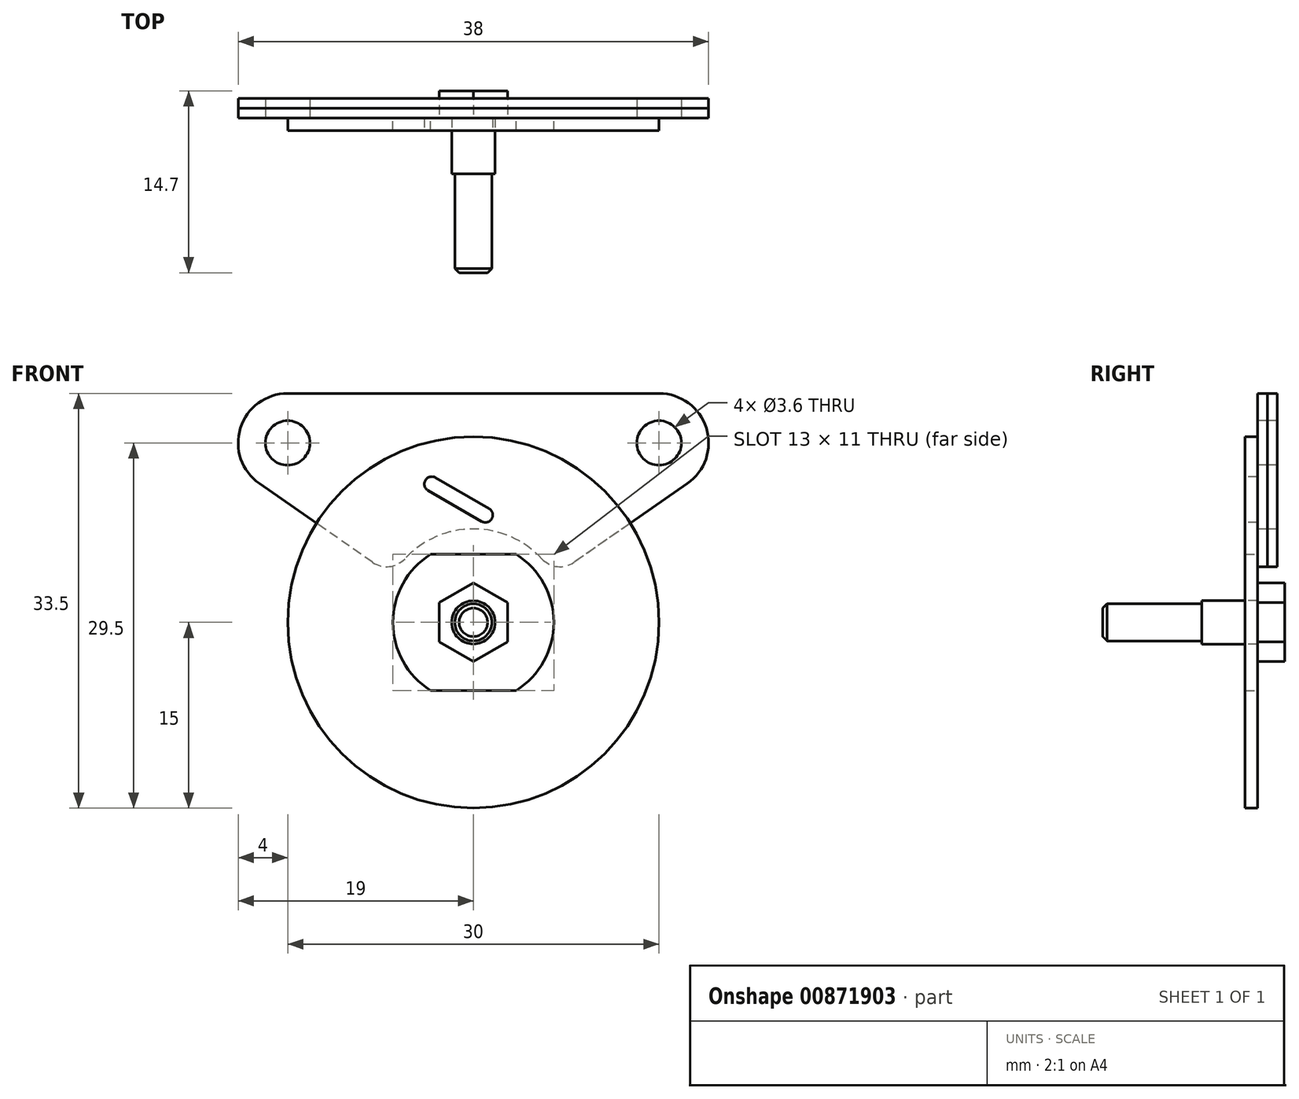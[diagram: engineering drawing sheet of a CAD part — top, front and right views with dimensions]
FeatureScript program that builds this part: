
annotation { "Feature Type Name" : "Feature", "Feature Type Description" : "" }
export const myFeature = defineFeature(function(context is Context, id is Id, definition is map)
    precondition{}
    {
        {
            var Q0;
            Q0=qCreatedBy(makeId("Front.planeOp"),FACE);
            var sketch = newSketch(context, id + "F0", { "sketchPlane" : qUnion([Q0])});
            skCircle(sketch, "E0", {"center": v(0, 0) * mm, "radius": 15 * mm});
            skArc(sketch, "E1", {"start": v(-3.46, 5.5) * mm, "mid": v(-6.5, 0) * mm, "end": v(-3.46, -5.5) * mm});
            skLineSegment(sketch, "E2", {"start": v(0, 0) * mm, "end": v(-24.22, 0) * mm, "construction": true});
            skLineSegment(sketch, "E3", {"start": v(-3.46, 5.5) * mm, "end": v(3.46, 5.5) * mm});
            skLineSegment(sketch, "E4", {"start": v(3.46, -5.5) * mm, "end": v(-3.46, -5.5) * mm});
            skArc(sketch, "E5.trimOffspring", {"start": v(3.46, -5.5) * mm, "mid": v(6.5, 0) * mm, "end": v(3.46, 5.5) * mm});
            skSolve(sketch);
        }
        {
            var Q0;
            Q0=qSketchRegion(id+"F0",true);
            extrude(context, id + "F1", {"entities" : qUnion([Q0]), "depth" : 1 * mm, "offsetDistance" : 25 * mm});
        }
        {
            var Q0;
            Q0=makeQuery(id+"F1.opExtrude","CAP_FACE",FACE,{"disambiguationData":[OSD([sQuery(id+"F0.wireOp",EDGE,"E0"),sQuery(id+"F0.wireOp",EDGE,"E1"),sQuery(id+"F0.wireOp",EDGE,"E3"),sQuery(id+"F0.wireOp",EDGE,"E4"),sQuery(id+"F0.wireOp",EDGE,"E5.trimOffspring")])],"isStart":false});
            var sketch = newSketch(context, id + "F2", { "sketchPlane" : qUnion([Q0])});
            skLineSegment(sketch, "E6", {"start": v(-3.36, 11.18) * mm, "end": v(0.97, 8.68) * mm, "construction": true});
            skArc(sketch, "E7.0.startCap", {"start": v(-3.66, 10.66) * mm, "mid": v(-3.88, 11.48) * mm, "end": v(-3.06, 11.7) * mm});
            skArc(sketch, "E7.0.endCap", {"start": v(1.27, 9.2) * mm, "mid": v(1.49, 8.38) * mm, "end": v(0.67, 8.16) * mm});
            skLineSegment(sketch, "E7.0.left", {"start": v(-3.06, 11.7) * mm, "end": v(1.27, 9.2) * mm});
            skLineSegment(sketch, "E7.0.right", {"start": v(-3.66, 10.66) * mm, "end": v(0.67, 8.16) * mm});
            skLineSegment(sketch, "E8", {"start": v(-1.2, 9.93) * mm, "end": v(-2.05, 8.46) * mm, "construction": true});
            skSolve(sketch);
        }
        {
            var Q0;
            Q0=qSketchRegion(id+"F2",true);
            extrude(context, id + "F3", {"entities" : qUnion([Q0]), "operationType" : NewBodyOperationType.REMOVE, "oppositeDirection" : true, "depth" : 25 * mm, "offsetDistance" : 25 * mm});
        }
        {
            var Q0;
            Q0=qCreatedBy(makeId("Front.planeOp"),FACE);
            var sketch = newSketch(context, id + "F4", { "sketchPlane" : qUnion([Q0])});
            skLineSegment(sketch, "E9", {"start": v(15, 14.5) * mm, "end": v(-15, 14.5) * mm, "construction": true});
            skLineSegment(sketch, "E10", {"start": v(7, 6.5) * mm, "end": v(-7, 6.5) * mm, "construction": true});
            skArc(sketch, "E11", {"start": v(17.28, 11.22) * mm, "mid": v(18.82, 15.7) * mm, "end": v(15, 18.5) * mm});
            skArc(sketch, "E12", {"start": v(-15, 18.5) * mm, "mid": v(-18.82, 15.7) * mm, "end": v(-17.28, 11.22) * mm});
            skArc(sketch, "E13", {"start": v(-8.14, 4.86) * mm, "mid": v(-6.79, 4.51) * mm, "end": v(-5.53, 5.14) * mm});
            skArc(sketch, "E14", {"start": v(5.53, 5.14) * mm, "mid": v(6.79, 4.51) * mm, "end": v(8.14, 4.86) * mm});
            skCircle(sketch, "E15", {"center": v(15, 14.5) * mm, "radius": 1.8 * mm});
            skCircle(sketch, "E16", {"center": v(-15, 14.5) * mm, "radius": 1.8 * mm});
            skLineSegment(sketch, "E17", {"start": v(15, 14.5) * mm, "end": v(15, 18.5) * mm, "construction": true});
            skLineSegment(sketch, "E18", {"start": v(15, 18.5) * mm, "end": v(-15, 18.5) * mm});
            skLineSegment(sketch, "E19", {"start": v(-15, 18.5) * mm, "end": v(-15, 14.5) * mm, "construction": true});
            skArc(sketch, "E20", {"start": v(5.53, 5.14) * mm, "mid": v(0, 7.55) * mm, "end": v(-5.53, 5.14) * mm});
            skLineSegment(sketch, "E21", {"start": v(0, 14.5) * mm, "end": v(0, 6.5) * mm, "construction": true});
            skLineSegment(sketch, "E22", {"start": v(17.28, 11.22) * mm, "end": v(8.14, 4.86) * mm});
            skLineSegment(sketch, "E23", {"start": v(-8.14, 4.86) * mm, "end": v(-17.28, 11.22) * mm});
            skSolve(sketch);
        }
        {
            var Q0;
            Q0=qSketchRegion(id+"F4",true);
            extrude(context, id + "F5", {"entities" : qUnion([Q0]), "oppositeDirection" : true, "depth" : 0.8 * mm, "offsetDistance" : 25 * mm});
        }
        {
            var Q0;
            Q0=makeQuery(id+"F5.opExtrude","SWEPT_BODY",BODY,{"disambiguationData":[OSD([sQuery(id+"F4.wireOp",EDGE,"E11"),sQuery(id+"F4.wireOp",EDGE,"E12"),sQuery(id+"F4.wireOp",EDGE,"E13"),sQuery(id+"F4.wireOp",EDGE,"E14"),sQuery(id+"F4.wireOp",EDGE,"E15"),sQuery(id+"F4.wireOp",EDGE,"E16"),sQuery(id+"F4.wireOp",EDGE,"E18"),sQuery(id+"F4.wireOp",EDGE,"E20"),sQuery(id+"F4.wireOp",EDGE,"E22"),sQuery(id+"F4.wireOp",EDGE,"E23")])]});
            transform(context, id + "F6", {"entities" : qUnion([Q0]), "transformType" : TransformType.TRANSLATION_3D, "dx" : 0 * mm, "dy" : 0.8 * mm, "dz" : 0 * mm, "makeCopy" : true});
        }
        {
            var Q0;
            Q0=qCreatedBy(makeId("Top.planeOp"),FACE);
            var sketch = newSketch(context, id + "F7", { "sketchPlane" : qUnion([Q0])});
            skLineSegment(sketch, "E24", {"start": v(0, 0) * mm, "end": v(0, -12.5) * mm});
            skLineSegment(sketch, "E25", {"start": v(0, -12.5) * mm, "end": v(-1.5, -12.5) * mm});
            skLineSegment(sketch, "E26", {"start": v(-1.5, -12.5) * mm, "end": v(-1.5, -4.5) * mm});
            skLineSegment(sketch, "E27", {"start": v(-1.5, -4.5) * mm, "end": v(-1.75, -4.5) * mm});
            skLineSegment(sketch, "E28", {"start": v(-1.75, -4.5) * mm, "end": v(-1.75, 0) * mm});
            skLineSegment(sketch, "E29", {"start": v(-1.75, 0) * mm, "end": v(0, 0) * mm});
            skLineSegment(sketch, "E30", {"start": v(0, 0) * mm, "end": v(0, 0.89) * mm, "construction": true});
            skSolve(sketch);
        }
        {
            var Q0;
            Q0=qSketchRegion(id+"F7",true);
            var Q1;
            Q1=sQuery(id+"F7.wireOp",EDGE,"E30");
            revolve(context, id + "F8", {"surfaceOperationType" : NewSurfaceOperationType.NEW, "entities" : qUnion([Q0]), "axis" : qUnion([Q1]), "revolveType" : RevolveType.FULL});
        }
        {
            var Q0;
            Q0=makeQuery(id+"F8.opRevolve","SWEPT_FACE",FACE,{"disambiguationData":[OSD([sQuery(id+"F7.wireOp",EDGE,"E29")])]});
            var sketch = newSketch(context, id + "F9", { "sketchPlane" : qUnion([Q0])});
            skCircle(sketch, "E31.cCircle", {"center": v(0, 0) * mm, "radius": 2.75 * mm, "construction": true});
            skLineSegment(sketch, "E31.0", {"start": v(2.75, 1.59) * mm, "end": v(2.75, -1.59) * mm});
            skLineSegment(sketch, "E31.1", {"start": v(2.75, -1.59) * mm, "end": v(0, -3.18) * mm});
            skLineSegment(sketch, "E31.2", {"start": v(0, -3.18) * mm, "end": v(-2.75, -1.59) * mm});
            skLineSegment(sketch, "E31.3", {"start": v(-2.75, -1.59) * mm, "end": v(-2.75, 1.59) * mm});
            skLineSegment(sketch, "E31.4", {"start": v(-2.75, 1.59) * mm, "end": v(0, 3.18) * mm});
            skLineSegment(sketch, "E31.5", {"start": v(0, 3.18) * mm, "end": v(2.75, 1.59) * mm});
            skPoint(sketch, "E31.0.midPoint", {"position": v(2.75, 0) * mm});
            skSolve(sketch);
        }
        {
            var Q0;
            Q0=qSketchRegion(id+"F9",true);
            extrude(context, id + "F10", {"entities" : qUnion([Q0]), "operationType" : NewBodyOperationType.ADD, "depth" : 2.2 * mm, "offsetDistance" : 25 * mm});
        }
        {
            var Q0;
            Q0=makeQuery(id+"F8.opRevolve","SWEPT_EDGE",EDGE,{"disambiguationData":[OSD([sQuery(id+"F7.wireOp",EDGE,"E25"),sQuery(id+"F7.wireOp",EDGE,"E26")])]});
            chamfer(context, id + "F11", {"entities" : qUnion([Q0]), "width" : 0.35 * mm, "tangentPropagation" : true});
        }
    });
